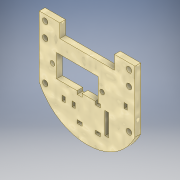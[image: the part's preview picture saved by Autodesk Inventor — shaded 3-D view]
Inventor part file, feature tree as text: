
AUTODESK INVENTOR PART (.ipt)
format: ipt  version: 2017 (Build 210142000, 142)  size: 195,584 bytes
history: native  units: in
note: dims shown in document units (in); Inventor stores cm internally (conversion verified against a paired STEP export)
features: extrude x1, sketch x1
ambient origin geometry x8: Origin, YZ Plane, XZ Plane, XY Plane, X Axis, Y Axis, Z Axis, Center Point
bodies: Solid1 (feature_tree)
feature tree (2):
  extrude  "Extrusion1"  Depth=1.35in
  sketch  "Sketch1"  dims[d0=1.16in d1=1.35in d2=0.45in d3=0.3in d4=1.2in d5=0.11in d6=0.5in d7=0.91in d8=0.3in d9=0.38in d10=0.07in d11=0.51in d12=0.17in d13=0.48in d14=0.29in d15=0.08in d16=0.1in d17=0.05in d18=0.04in d19=0.18in d20=0.15in d21=0.12in d22=0.1in d23=0.13in d24=0.13in d25=0.13in d26=0.13in d27=0.32in d28=0.86in d29=0.09in d30=0.09in d31=0.25in d32=0.125in d33=0.0in]
